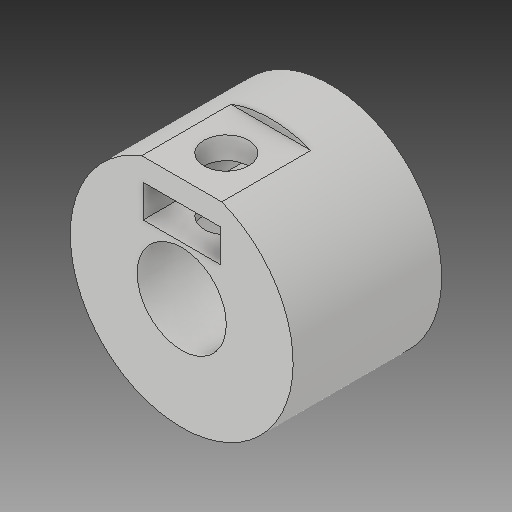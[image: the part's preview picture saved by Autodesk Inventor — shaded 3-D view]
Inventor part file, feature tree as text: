
AUTODESK INVENTOR PART (.ipt)
format: ipt  version: 2019 (Build 230136000, 136)  size: 143,872 bytes
history: native  units: mm
features: sketch x5, extrude x4, plane x1
ambient origin geometry x8: Origin, YZ Plane, XZ Plane, XY Plane, X Axis, Y Axis, Z Axis, Center Point
bodies: Solid1 (feature_tree)
feature tree (10):
  extrude  "Extrusion1"  Depth=6.0mm
  plane  "Work Plane1"
  extrude  "Extrusion2"  Depth=10.0mm
  extrude  "Extrusion3"  Depth=2.2mm
  extrude  "Extrusion4"  Depth=7.0mm TaperAngle=0.0deg
  sketch  "Sketch6"  dims[d12=3.0mm d13=7.0mm d14=8.0mm d15=0.0mm d16=6.0mm d17=10.0mm d18=0.5mm d19=8.0mm d20=0.0mm]
  sketch  "Sketch1"  dims[d0=15.0mm d1=6.0mm]
  sketch  "Sketch2"  dims[d2=10.0mm d3=0.0mm d4=3.0mm]
  sketch  "Sketch4"  dims[d5=5.5mm d6=2.2mm]
  sketch  "Sketch5"  dims[d7=5.2mm d8=7.0mm d9=0.0mm]
